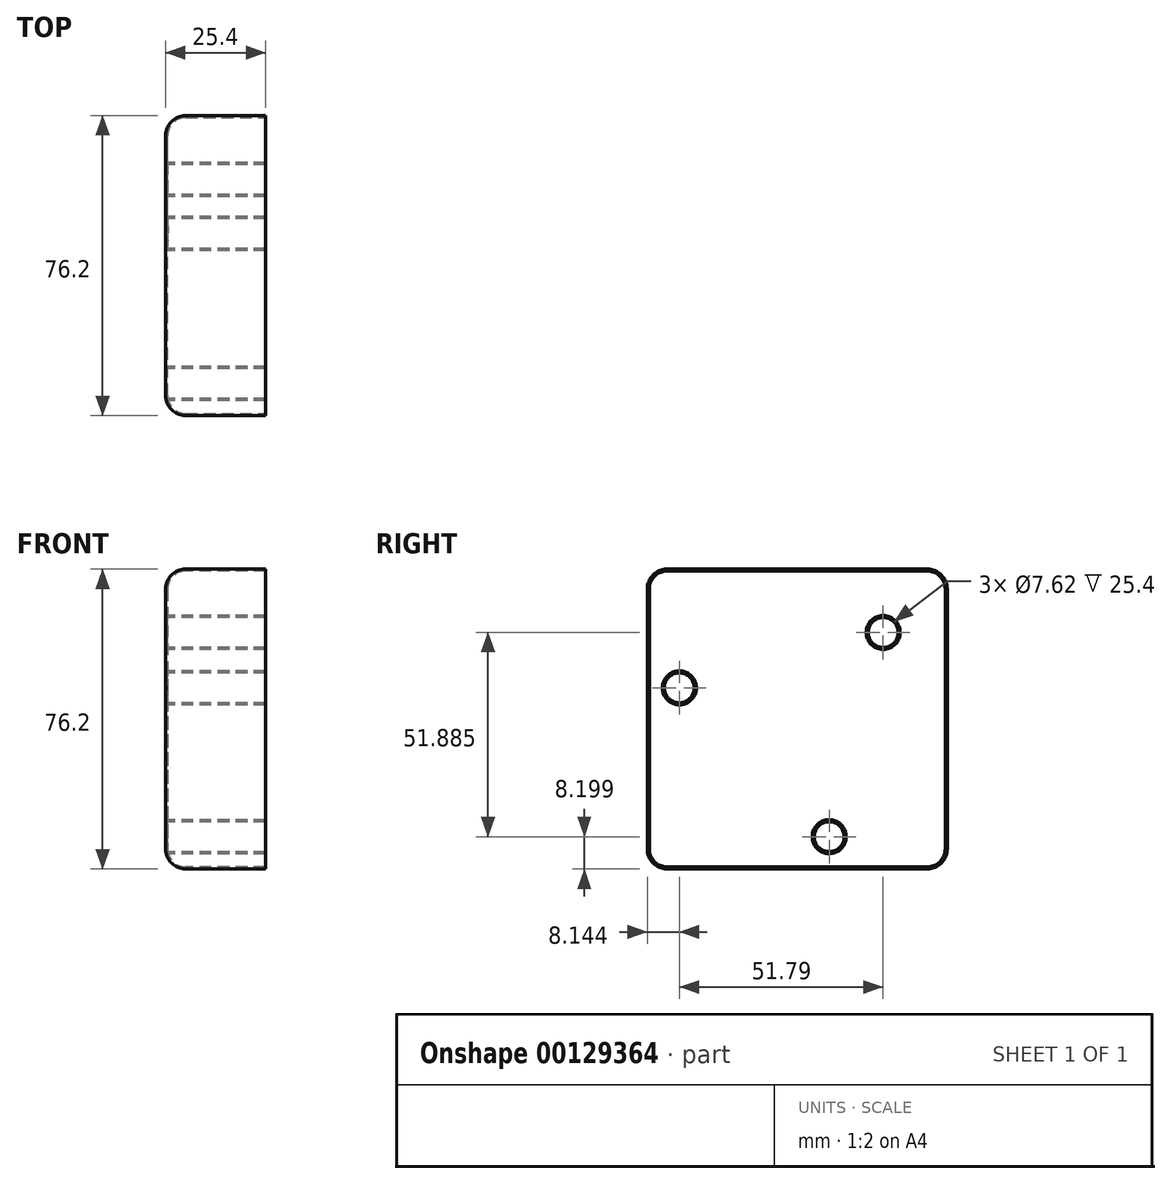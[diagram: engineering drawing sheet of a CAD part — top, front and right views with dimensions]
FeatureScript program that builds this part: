
annotation { "Feature Type Name" : "Feature", "Feature Type Description" : "" }
export const myFeature = defineFeature(function(context is Context, id is Id, definition is map)
    precondition{}
    {
        {
            var Q0;
            Q0=qCreatedBy(makeId("Front.planeOp"),FACE);
            var sketch = newSketch(context, id + "F0", { "sketchPlane" : qUnion([Q0])});
            skLineSegment(sketch, "E0.bottom", {"start": v(12.7, 38.1) * mm, "end": v(-12.7, 38.1) * mm});
            skLineSegment(sketch, "E0.top", {"start": v(12.7, -38.1) * mm, "end": v(-12.7, -38.1) * mm});
            skLineSegment(sketch, "E0.left", {"start": v(12.7, 38.1) * mm, "end": v(12.7, -38.1) * mm});
            skLineSegment(sketch, "E0.right", {"start": v(-12.7, 38.1) * mm, "end": v(-12.7, -38.1) * mm});
            skPoint(sketch, "E0.middle", {"position": v(0, 0) * mm});
            skSolve(sketch);
        }
        {
            var Q0;
            Q0=makeQuery(id+"F0.imprint","IMPRINT",FACE,{"disambiguationData":[TD([[makeQuery(id+"F0.imprint","IMPRINT",EDGE,{"derivedFrom":sQuery(id+"F0.wireOp",EDGE,"E0.bottom")}),1.0]])]});
            extrude(context, id + "F1", {"entities" : qUnion([Q0]), "endBound" : BoundingType.SYMMETRIC, "depth" : 76.2 * mm});
        }
        {
            var Q0;
            Q0=makeQuery(id+"F1.opExtrude","SWEPT_FACE",FACE,{"disambiguationData":[OSD([sQuery(id+"F0.wireOp",EDGE,"E0.right")])]});
            var sketch = newSketch(context, id + "F2", { "sketchPlane" : qUnion([Q0])});
            skCircle(sketch, "E1", {"center": v(-21.83, 21.98) * mm, "radius": 6.35 * mm});
            skCircle(sketch, "E2.1.0", {"center": v(-8.12, -29.9) * mm, "radius": 6.35 * mm});
            skCircle(sketch, "E2.2.0", {"center": v(29.96, 7.92) * mm, "radius": 6.35 * mm});
            skPoint(sketch, "E2.center", {"position": v(0, 0) * mm});
            skSolve(sketch);
        }
        {
            var Q0;
            Q0=sQuery(id+"F2.wireOp",VERTEX,"E2.2.0.center");
            var Q1;
            Q1=sQuery(id+"F2.wireOp",VERTEX,"E1.center");
            var Q2;
            Q2=sQuery(id+"F2.wireOp",VERTEX,"E2.1.0.center");
            var Q3;
            Q3=makeQuery(id+"F1.opExtrude","SWEPT_BODY",BODY,{"disambiguationData":[OSD([sQuery(id+"F0.wireOp",EDGE,"E0.bottom"),sQuery(id+"F0.wireOp",EDGE,"E0.top"),sQuery(id+"F0.wireOp",EDGE,"E0.left"),sQuery(id+"F0.wireOp",EDGE,"E0.right")])]});
            hole(context, id + "F3", {"style" : HoleStyle.SIMPLE, "endStyle" : HoleEndStyle.THROUGH, "holeDiameter" : 7.62 * mm, "locations" : qUnion([Q0, Q1, Q2]), "scope" : qUnion([Q3]), "isTappedThrough" : true});
        }
        {
            var Q0;
            Q0=makeQuery(id+"F1.opExtrude","SWEPT_EDGE",EDGE,{"disambiguationData":[OSD([sQuery(id+"F0.wireOp",EDGE,"E0.bottom"),sQuery(id+"F0.wireOp",EDGE,"E0.right")])]});
            var Q1;
            Q1=makeQuery(id+"F1.opExtrude","CAP_EDGE",EDGE,{"disambiguationData":[OSD([sQuery(id+"F0.wireOp",EDGE,"E0.right")])],"isStart":true});
            var Q2;
            Q2=makeQuery(id+"F1.opExtrude","SWEPT_EDGE",EDGE,{"disambiguationData":[OSD([sQuery(id+"F0.wireOp",EDGE,"E0.top"),sQuery(id+"F0.wireOp",EDGE,"E0.right")])]});
            var Q3;
            Q3=makeQuery(id+"F1.opExtrude","CAP_EDGE",EDGE,{"disambiguationData":[OSD([sQuery(id+"F0.wireOp",EDGE,"E0.right")])],"isStart":false});
            var Q4;
            Q4=makeQuery(id+"F1.opExtrude","CAP_EDGE",EDGE,{"disambiguationData":[OSD([sQuery(id+"F0.wireOp",EDGE,"E0.bottom")])],"isStart":true});
            var Q5;
            Q5=makeQuery(id+"F1.opExtrude","CAP_EDGE",EDGE,{"disambiguationData":[OSD([sQuery(id+"F0.wireOp",EDGE,"E0.top")])],"isStart":true});
            var Q6;
            Q6=makeQuery(id+"F1.opExtrude","CAP_EDGE",EDGE,{"disambiguationData":[OSD([sQuery(id+"F0.wireOp",EDGE,"E0.bottom")])],"isStart":false});
            var Q7;
            Q7=makeQuery(id+"F1.opExtrude","CAP_EDGE",EDGE,{"disambiguationData":[OSD([sQuery(id+"F0.wireOp",EDGE,"E0.top")])],"isStart":false});
            fillet(context, id + "F4", {"entities" : qUnion([Q0, Q1, Q2, Q3, Q4, Q5, Q6, Q7]), "radius" : 5.08 * mm, "tangentPropagation" : true, "allowEdgeOverflow" : false});
        }
        {
            var Q0;
            Q0=makeQuery(id+"F1.opExtrude","SWEPT_FACE",FACE,{"disambiguationData":[OSD([sQuery(id+"F0.wireOp",EDGE,"E0.left")])]});
            shell(context, id + "F5", {"entities" : qUnion([Q0]), "thickness" : 0.5 * mm});
        }
    });
